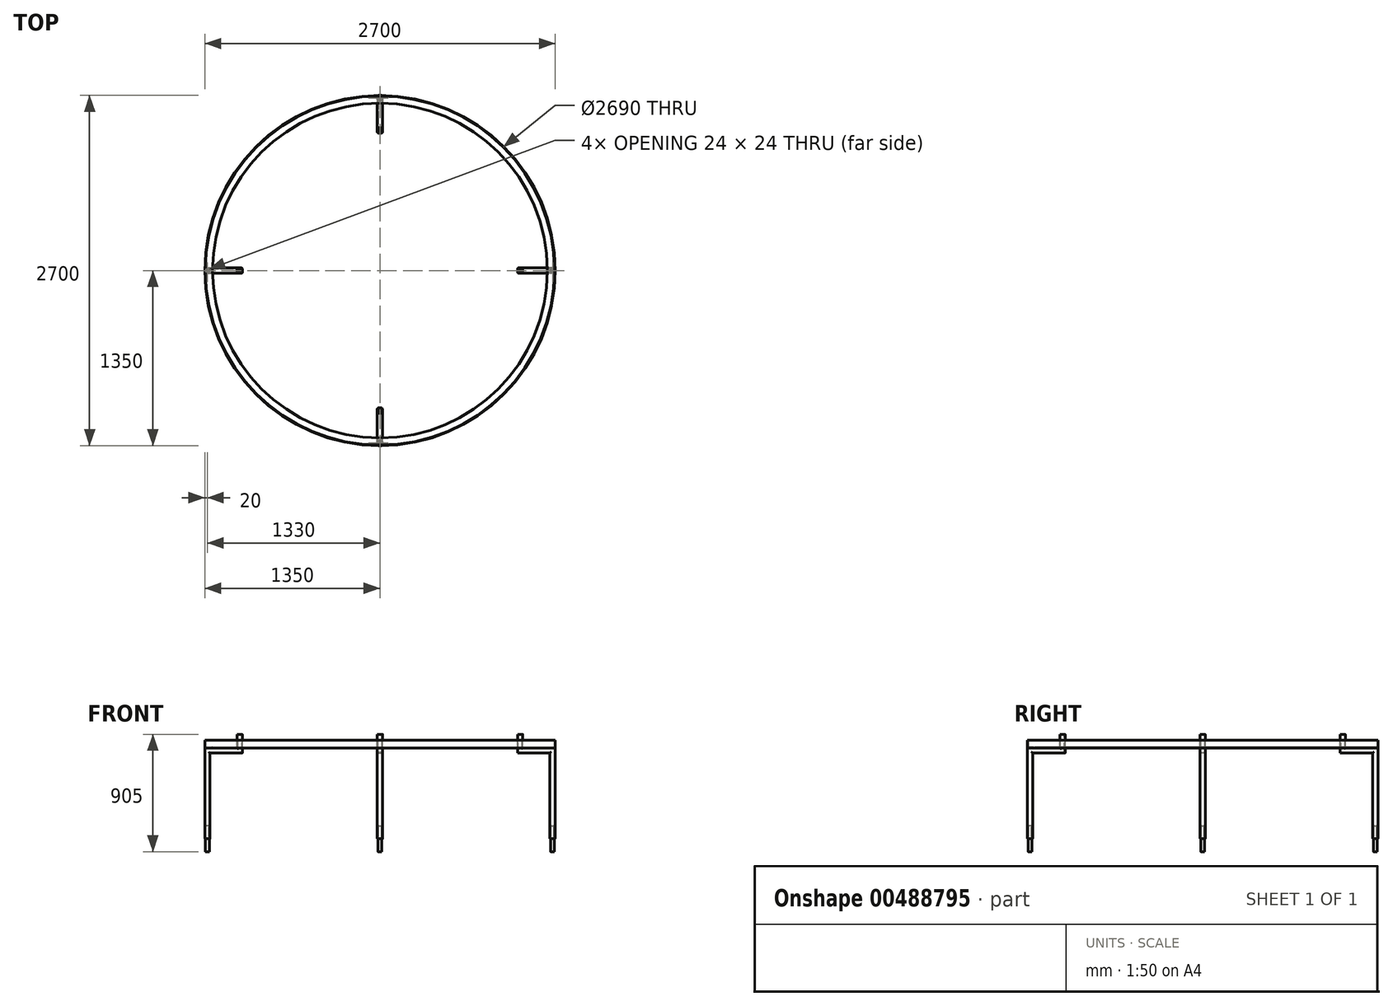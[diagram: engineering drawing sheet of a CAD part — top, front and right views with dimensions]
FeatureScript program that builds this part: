
annotation { "Feature Type Name" : "Feature", "Feature Type Description" : "" }
export const myFeature = defineFeature(function(context is Context, id is Id, definition is map)
    precondition{}
    {
        {
            var Q0;
            Q0=qCreatedBy(makeId("Front.planeOp"),FACE);
            var sketch = newSketch(context, id + "F0", { "sketchPlane" : qUnion([Q0])});
            skLineSegment(sketch, "E0", {"start": v(0, 0) * mm, "end": v(0, 129.65) * mm, "construction": true});
            skLineSegment(sketch, "E1", {"start": v(1290, 0) * mm, "end": v(1350, 0) * mm});
            skLineSegment(sketch, "E2", {"start": v(1350, 0) * mm, "end": v(1350, 60) * mm});
            skLineSegment(sketch, "E3.0", {"start": v(1345, 10) * mm, "end": v(1345, 55) * mm});
            skLineSegment(sketch, "E3.1", {"start": v(1295, 5) * mm, "end": v(1340, 5) * mm});
            skLineSegment(sketch, "E4", {"start": v(1350, 60) * mm, "end": v(1350, 60) * mm});
            skLineSegment(sketch, "E5", {"start": v(1290, 0) * mm, "end": v(1290, 0) * mm});
            skPoint(sketch, "E6.visualSharp", {"position": v(1345, 5) * mm});
            skArc(sketch, "E6.filletArc", {"start": v(1340, 5) * mm, "mid": v(1343.54, 6.46) * mm, "end": v(1345, 10) * mm});
            skPoint(sketch, "E7.visualSharp", {"position": v(1345, 60) * mm});
            skArc(sketch, "E7.filletArc", {"start": v(1350, 60) * mm, "mid": v(1346.46, 58.54) * mm, "end": v(1345, 55) * mm});
            skPoint(sketch, "E8.visualSharp", {"position": v(1290, 5) * mm});
            skArc(sketch, "E8.filletArc", {"start": v(1295, 5) * mm, "mid": v(1291.46, 3.54) * mm, "end": v(1290, 0) * mm});
            skSolve(sketch);
        }
        {
            var Q0;
            Q0=makeQuery(id+"F0.imprint","IMPRINT",FACE,{"disambiguationData":[TD([[makeQuery(id+"F0.imprint","IMPRINT",EDGE,{"derivedFrom":sQuery(id+"F0.wireOp",EDGE,"E1")}),1.0]])]});
            var Q1;
            Q1=sQuery(id+"F0.wireOp",EDGE,"E0");
            revolve(context, id + "F1", {"entities" : qUnion([Q0]), "axis" : qUnion([Q1]), "revolveType" : RevolveType.FULL});
        }
        {
            var Q0;
            Q0=qCreatedBy(makeId("Right.planeOp"),FACE);
            var sketch = newSketch(context, id + "F2", { "sketchPlane" : qUnion([Q0])});
            skLineSegment(sketch, "E9", {"start": v(-1505, -270) * mm, "end": v(-1330, -270) * mm});
            skLineSegment(sketch, "E10", {"start": v(-1330, -270) * mm, "end": v(-1330, -20) * mm});
            skLineSegment(sketch, "E11", {"start": v(-1330, -20) * mm, "end": v(-1080, -20) * mm});
            skLineSegment(sketch, "E12", {"start": v(-1080, -20) * mm, "end": v(-1080, 105) * mm});
            skSolve(sketch);
        }
        {
            var Q0;
            Q0=qCreatedBy(makeId("Front.planeOp"),FACE);
            var Q1;
            Q1=sQuery(id+"F2.wireOp",VERTEX,"E9.start");
            cPlane(context, id + "F3", {"entities" : qUnion([Q0, Q1]), "cplaneType" : CPlaneType.PLANE_POINT, "offset" : 25 * mm, "width" : 150 * mm, "height" : 150 * mm});
        }
        {
            var Q0;
            Q0=qCreatedBy(id+"F3.planeOp",FACE);
            var sketch = newSketch(context, id + "F4", { "sketchPlane" : qUnion([Q0])});
            skLineSegment(sketch, "E13.bottom", {"start": v(12, -290) * mm, "end": v(-12, -290) * mm});
            skLineSegment(sketch, "E13.top", {"start": v(12, -250) * mm, "end": v(-12, -250) * mm});
            skLineSegment(sketch, "E13.left", {"start": v(20, -282) * mm, "end": v(20, -258) * mm});
            skLineSegment(sketch, "E13.right", {"start": v(-20, -282) * mm, "end": v(-20, -258) * mm});
            skPoint(sketch, "E13.middle", {"position": v(0, -270) * mm});
            skPoint(sketch, "E14.visualSharp", {"position": v(-20, -250) * mm});
            skArc(sketch, "E14.filletArc", {"start": v(-12, -250) * mm, "mid": v(-17.66, -252.34) * mm, "end": v(-20, -258) * mm});
            skPoint(sketch, "E15.visualSharp", {"position": v(20, -250) * mm});
            skArc(sketch, "E15.filletArc", {"start": v(20, -258) * mm, "mid": v(17.66, -252.34) * mm, "end": v(12, -250) * mm});
            skPoint(sketch, "E16.visualSharp", {"position": v(20, -290) * mm});
            skArc(sketch, "E16.filletArc", {"start": v(12, -290) * mm, "mid": v(17.66, -287.66) * mm, "end": v(20, -282) * mm});
            skPoint(sketch, "E17.visualSharp", {"position": v(-20, -290) * mm});
            skArc(sketch, "E17.filletArc", {"start": v(-20, -282) * mm, "mid": v(-17.66, -287.66) * mm, "end": v(-12, -290) * mm});
            skArc(sketch, "E18.0", {"start": v(16, -258) * mm, "mid": v(14.83, -255.17) * mm, "end": v(12, -254) * mm});
            skLineSegment(sketch, "E18.1", {"start": v(16, -282) * mm, "end": v(16, -258) * mm});
            skLineSegment(sketch, "E18.2", {"start": v(12, -254) * mm, "end": v(-12, -254) * mm});
            skArc(sketch, "E18.3", {"start": v(12, -286) * mm, "mid": v(14.83, -284.83) * mm, "end": v(16, -282) * mm});
            skArc(sketch, "E18.4", {"start": v(-12, -254) * mm, "mid": v(-14.83, -255.17) * mm, "end": v(-16, -258) * mm});
            skLineSegment(sketch, "E18.5", {"start": v(-16, -282) * mm, "end": v(-16, -258) * mm});
            skArc(sketch, "E18.6", {"start": v(-16, -282) * mm, "mid": v(-14.83, -284.83) * mm, "end": v(-12, -286) * mm});
            skLineSegment(sketch, "E18.7", {"start": v(12, -286) * mm, "end": v(-12, -286) * mm});
            skSolve(sketch);
        }
        {
            var Q0;
            Q0=makeQuery(id+"F4.imprint","IMPRINT",FACE,{"disambiguationData":[TD([[makeQuery(id+"F4.imprint","IMPRINT",EDGE,{"derivedFrom":sQuery(id+"F4.wireOp",EDGE,"E13.bottom")}),-1.0]])]});
            var Q1;
            Q1=sQuery(id+"F2.wireOp",EDGE,"E9");
            var Q2;
            Q2=sQuery(id+"F2.wireOp",EDGE,"E10");
            var Q3;
            Q3=sQuery(id+"F2.wireOp",EDGE,"E11");
            var Q4;
            Q4=sQuery(id+"F2.wireOp",EDGE,"E12");
            sweep(context, id + "F5", {"profiles" : qUnion([Q0]), "path" : qUnion([Q1, Q2, Q3, Q4])});
        }
        {
            var Q0;
            Q0=makeQuery(id+"F5.opSweep","SWEPT_FACE",FACE,{"disambiguationData":[OSD([sQuery(id+"F2.wireOp",EDGE,"E9"),sQuery(id+"F4.wireOp",EDGE,"E13.right")])]});
            var sketch = newSketch(context, id + "F6", { "sketchPlane" : qUnion([Q0])});
            skLineSegment(sketch, "E19.bottom", {"start": v(1505, -250) * mm, "end": v(1310, -250) * mm});
            skLineSegment(sketch, "E19.top", {"start": v(1505, -290) * mm, "end": v(1310, -290) * mm});
            skLineSegment(sketch, "E19.left", {"start": v(1505, -250) * mm, "end": v(1505, -290) * mm});
            skLineSegment(sketch, "E19.right", {"start": v(1310, -250) * mm, "end": v(1310, -290) * mm});
            skSolve(sketch);
        }
        {
            var Q0;
            Q0=qSketchRegion(id+"F6",true);
            extrude(context, id + "F7", {"entities" : qUnion([Q0]), "operationType" : NewBodyOperationType.REMOVE, "endBound" : BoundingType.THROUGH_ALL, "oppositeDirection" : true, "depth" : 25 * mm});
        }
        {
            var Q0;
            Q0=makeQuery(id+"F7.boolean.opBoolean","COPY",FACE,{"derivedFrom":makeQuery(id+"F7.opExtrude","SWEPT_FACE",FACE,{"disambiguationData":[OSD([sQuery(id+"F6.wireOp",EDGE,"E19.bottom")])]})});
            var sketch = newSketch(context, id + "F8", { "sketchPlane" : qUnion([Q0])});
            skArc(sketch, "E20.0", {"start": v(20, 1342) * mm, "mid": v(17.66, 1347.66) * mm, "end": v(12, 1350) * mm});
            skLineSegment(sketch, "E20.1", {"start": v(20, 1318) * mm, "end": v(20, 1342) * mm});
            skLineSegment(sketch, "E20.2", {"start": v(12, 1350) * mm, "end": v(-12, 1350) * mm});
            skArc(sketch, "E20.3", {"start": v(12, 1310) * mm, "mid": v(17.66, 1312.34) * mm, "end": v(20, 1318) * mm});
            skLineSegment(sketch, "E20.4", {"start": v(12, 1310) * mm, "end": v(-12, 1310) * mm});
            skArc(sketch, "E20.5", {"start": v(-20, 1318) * mm, "mid": v(-17.66, 1312.34) * mm, "end": v(-12, 1310) * mm});
            skLineSegment(sketch, "E20.6", {"start": v(-20, 1342) * mm, "end": v(-20, 1318) * mm});
            skArc(sketch, "E20.7", {"start": v(-12, 1350) * mm, "mid": v(-17.66, 1347.66) * mm, "end": v(-20, 1342) * mm});
            skLineSegment(sketch, "E20.8", {"start": v(-12, 1346) * mm, "end": v(12, 1346) * mm});
            skArc(sketch, "E20.9", {"start": v(12, 1346) * mm, "mid": v(14.83, 1344.83) * mm, "end": v(16, 1342) * mm});
            skLineSegment(sketch, "E20.10", {"start": v(16, 1342) * mm, "end": v(16, 1318) * mm});
            skArc(sketch, "E20.11", {"start": v(16, 1318) * mm, "mid": v(14.83, 1315.17) * mm, "end": v(12, 1314) * mm});
            skLineSegment(sketch, "E20.12", {"start": v(12, 1314) * mm, "end": v(-12, 1314) * mm});
            skArc(sketch, "E20.13", {"start": v(-12, 1314) * mm, "mid": v(-14.83, 1315.17) * mm, "end": v(-16, 1318) * mm});
            skLineSegment(sketch, "E20.14", {"start": v(-16, 1318) * mm, "end": v(-16, 1342) * mm});
            skArc(sketch, "E20.15", {"start": v(-16, 1342) * mm, "mid": v(-14.83, 1344.83) * mm, "end": v(-12, 1346) * mm});
            skSolve(sketch);
        }
        {
            var Q0;
            Q0=qSketchRegion(id+"F8",true);
            extrude(context, id + "F9", {"entities" : qUnion([Q0]), "operationType" : NewBodyOperationType.ADD, "depth" : 450 * mm});
        }
        {
            var Q0;
            Q0=makeQuery(id+"F9.opExtrude","CAP_FACE",FACE,{"disambiguationData":[OSD([sQuery(id+"F8.wireOp",EDGE,"E20.0"),sQuery(id+"F8.wireOp",EDGE,"E20.1"),sQuery(id+"F8.wireOp",EDGE,"E20.2"),sQuery(id+"F8.wireOp",EDGE,"E20.3"),sQuery(id+"F8.wireOp",EDGE,"E20.4"),sQuery(id+"F8.wireOp",EDGE,"E20.5"),sQuery(id+"F8.wireOp",EDGE,"E20.6"),sQuery(id+"F8.wireOp",EDGE,"E20.7"),sQuery(id+"F8.wireOp",EDGE,"E20.8"),sQuery(id+"F8.wireOp",EDGE,"E20.9"),sQuery(id+"F8.wireOp",EDGE,"E20.10"),sQuery(id+"F8.wireOp",EDGE,"E20.11"),sQuery(id+"F8.wireOp",EDGE,"E20.12"),sQuery(id+"F8.wireOp",EDGE,"E20.13"),sQuery(id+"F8.wireOp",EDGE,"E20.14"),sQuery(id+"F8.wireOp",EDGE,"E20.15")])],"isStart":false});
            var sketch = newSketch(context, id + "F10", { "sketchPlane" : qUnion([Q0])});
            skLineSegment(sketch, "E21.bottom", {"start": v(9, 1315) * mm, "end": v(-9, 1315) * mm});
            skLineSegment(sketch, "E21.top", {"start": v(9, 1345) * mm, "end": v(-9, 1345) * mm});
            skLineSegment(sketch, "E21.left", {"start": v(15, 1321) * mm, "end": v(15, 1339) * mm});
            skLineSegment(sketch, "E21.right", {"start": v(-15, 1321) * mm, "end": v(-15, 1339) * mm});
            skPoint(sketch, "E21.middle", {"position": v(0, 1330) * mm});
            skPoint(sketch, "E21.middle.positionSnap0", {"position": v(-20, 1330) * mm});
            skPoint(sketch, "E21.middle.positionSnap1", {"position": v(0, 1346) * mm});
            skPoint(sketch, "E21.centerSnap0", {"position": v(-20, 1330) * mm});
            skPoint(sketch, "E21.centerSnap1", {"position": v(0, 1346) * mm});
            skPoint(sketch, "E22.visualSharp", {"position": v(-15, 1345) * mm});
            skArc(sketch, "E22.filletArc", {"start": v(-9, 1345) * mm, "mid": v(-13.24, 1343.24) * mm, "end": v(-15, 1339) * mm});
            skPoint(sketch, "E23.visualSharp", {"position": v(15, 1345) * mm});
            skArc(sketch, "E23.filletArc", {"start": v(15, 1339) * mm, "mid": v(13.24, 1343.24) * mm, "end": v(9, 1345) * mm});
            skPoint(sketch, "E24.visualSharp", {"position": v(15, 1315) * mm});
            skArc(sketch, "E24.filletArc", {"start": v(9, 1315) * mm, "mid": v(13.24, 1316.76) * mm, "end": v(15, 1321) * mm});
            skPoint(sketch, "E25.visualSharp", {"position": v(-15, 1315) * mm});
            skArc(sketch, "E25.filletArc", {"start": v(-15, 1321) * mm, "mid": v(-13.24, 1316.76) * mm, "end": v(-9, 1315) * mm});
            skArc(sketch, "E26.0", {"start": v(9, 1318) * mm, "mid": v(11.12, 1318.88) * mm, "end": v(12, 1321) * mm});
            skLineSegment(sketch, "E26.1", {"start": v(9, 1318) * mm, "end": v(-9, 1318) * mm});
            skLineSegment(sketch, "E26.2", {"start": v(12, 1321) * mm, "end": v(12, 1339) * mm});
            skArc(sketch, "E26.3", {"start": v(-12, 1321) * mm, "mid": v(-11.12, 1318.88) * mm, "end": v(-9, 1318) * mm});
            skArc(sketch, "E26.4", {"start": v(12, 1339) * mm, "mid": v(11.12, 1341.12) * mm, "end": v(9, 1342) * mm});
            skLineSegment(sketch, "E26.5", {"start": v(9, 1342) * mm, "end": v(-9, 1342) * mm});
            skArc(sketch, "E26.6", {"start": v(-9, 1342) * mm, "mid": v(-11.12, 1341.12) * mm, "end": v(-12, 1339) * mm});
            skLineSegment(sketch, "E26.7", {"start": v(-12, 1321) * mm, "end": v(-12, 1339) * mm});
            skSolve(sketch);
        }
        {
            var Q0;
            Q0=qSketchRegion(id+"F10",true);
            extrude(context, id + "F11", {"entities" : qUnion([Q0]), "depth" : 100 * mm, "hasSecondDirection" : true, "secondDirectionOppositeDirection" : true, "secondDirectionDepth" : 100 * mm});
        }
        {
            var Q0;
            Q0=makeQuery(id+"F5.opSweep","SWEPT_BODY",BODY,{"disambiguationData":[OSD([sQuery(id+"F2.wireOp",EDGE,"E12"),sQuery(id+"F4.wireOp",EDGE,"E13.bottom"),sQuery(id+"F4.wireOp",EDGE,"E13.top"),sQuery(id+"F4.wireOp",EDGE,"E13.left"),sQuery(id+"F4.wireOp",EDGE,"E13.right"),sQuery(id+"F4.wireOp",EDGE,"E14.filletArc"),sQuery(id+"F4.wireOp",EDGE,"E15.filletArc"),sQuery(id+"F4.wireOp",EDGE,"E16.filletArc"),sQuery(id+"F4.wireOp",EDGE,"E17.filletArc"),sQuery(id+"F4.wireOp",EDGE,"E18.0"),sQuery(id+"F4.wireOp",EDGE,"E18.1"),sQuery(id+"F4.wireOp",EDGE,"E18.2"),sQuery(id+"F4.wireOp",EDGE,"E18.3"),sQuery(id+"F4.wireOp",EDGE,"E18.4"),sQuery(id+"F4.wireOp",EDGE,"E18.5"),sQuery(id+"F4.wireOp",EDGE,"E18.6"),sQuery(id+"F4.wireOp",EDGE,"E18.7")])]});
            var Q1;
            Q1=makeQuery(id+"F11.opExtrude","SWEPT_BODY",BODY,{"disambiguationData":[OSD([sQuery(id+"F10.wireOp",EDGE,"E21.bottom"),sQuery(id+"F10.wireOp",EDGE,"E21.top"),sQuery(id+"F10.wireOp",EDGE,"E21.left"),sQuery(id+"F10.wireOp",EDGE,"E21.right"),sQuery(id+"F10.wireOp",EDGE,"E22.filletArc"),sQuery(id+"F10.wireOp",EDGE,"E23.filletArc"),sQuery(id+"F10.wireOp",EDGE,"E24.filletArc"),sQuery(id+"F10.wireOp",EDGE,"E25.filletArc"),sQuery(id+"F10.wireOp",EDGE,"E26.0"),sQuery(id+"F10.wireOp",EDGE,"E26.1"),sQuery(id+"F10.wireOp",EDGE,"E26.2"),sQuery(id+"F10.wireOp",EDGE,"E26.3"),sQuery(id+"F10.wireOp",EDGE,"E26.4"),sQuery(id+"F10.wireOp",EDGE,"E26.5"),sQuery(id+"F10.wireOp",EDGE,"E26.6"),sQuery(id+"F10.wireOp",EDGE,"E26.7")])]});
            var Q2;
            Q2=makeQuery(id+"F1.opRevolve","SWEPT_EDGE",EDGE,{"disambiguationData":[OSD([sQuery(id+"F0.wireOp",EDGE,"E2"),sQuery(id+"F0.wireOp",EDGE,"E7.filletArc")])]});
            circularPattern(context, id + "F12", {"entities" : qUnion([Q0, Q1]), "axis" : qUnion([Q2]), "angle" : 360 * degree, "instanceCount" : 4, "equalSpace" : true});
        }
    });
